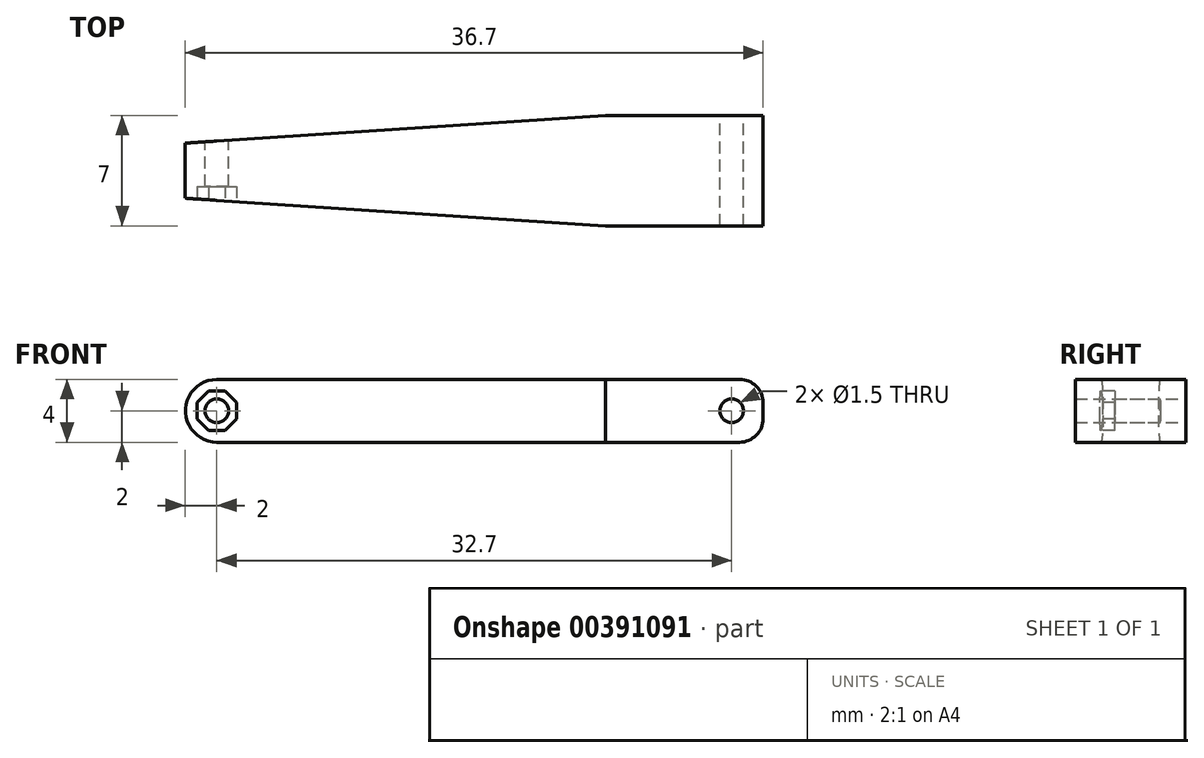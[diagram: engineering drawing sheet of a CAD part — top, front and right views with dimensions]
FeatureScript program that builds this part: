
annotation { "Feature Type Name" : "Feature", "Feature Type Description" : "" }
export const myFeature = defineFeature(function(context is Context, id is Id, definition is map)
    precondition{}
    {
        {
            var Q0;
            Q0=qCreatedBy(makeId("Top.planeOp"),FACE);
            var sketch = newSketch(context, id + "F0", { "sketchPlane" : qUnion([Q0])});
            skLineSegment(sketch, "E0.bottom", {"start": v(0, 0) * mm, "end": v(-36.7, 0) * mm});
            skLineSegment(sketch, "E0.top", {"start": v(0, -7) * mm, "end": v(-36.7, -7) * mm});
            skLineSegment(sketch, "E0.left", {"start": v(0, 0) * mm, "end": v(0, -7) * mm});
            skLineSegment(sketch, "E0.right", {"start": v(-36.7, 0) * mm, "end": v(-36.7, -7) * mm});
            skSolve(sketch);
        }
        {
            var Q0;
            Q0 = qSketchRegion(id + "F0", true);
            extrude(context, id + "F1", {"entities" : qUnion([Q0]), "depth" : 4 * mm});
        }
        {
            var Q0;
            Q0=makeQuery(id+"F1.opExtrude","CAP_FACE",FACE,{"disambiguationData":[OSD([sQuery(id+"F0.wireOp",EDGE,"E0.bottom"),sQuery(id+"F0.wireOp",EDGE,"E0.top"),sQuery(id+"F0.wireOp",EDGE,"E0.left"),sQuery(id+"F0.wireOp",EDGE,"E0.right")])],"isStart":false});
            var sketch = newSketch(context, id + "F2", { "sketchPlane" : qUnion([Q0])});
            skLineSegment(sketch, "E1", {"start": v(-36.7, -3.5) * mm, "end": v(0, -3.5) * mm, "construction": true});
            skLineSegment(sketch, "E2", {"start": v(0, 0) * mm, "end": v(-10, 0) * mm, "construction": true});
            skLineSegment(sketch, "E3", {"start": v(-36.7, -3.5) * mm, "end": v(-36.7, 0) * mm, "construction": true});
            skLineSegment(sketch, "E4", {"start": v(-36.7, -1.75) * mm, "end": v(-10, 0) * mm});
            skLineSegment(sketch, "E5.MirrorCS", {"start": v(-36.7, -5.25) * mm, "end": v(-10, -7) * mm});
            skLineSegment(sketch, "E6", {"start": v(-10, -7) * mm, "end": v(0, -7) * mm});
            skLineSegment(sketch, "E7", {"start": v(0, -7) * mm, "end": v(0, 0) * mm});
            skLineSegment(sketch, "E8", {"start": v(-36.7, -5.25) * mm, "end": v(-36.7, -1.75) * mm});
            skSolve(sketch);
        }
        {
            var Q0;
            Q0=makeQuery(id+"F1.opExtrude","SWEPT_FACE",FACE,{"disambiguationData":[OSD([sQuery(id+"F0.wireOp",EDGE,"E0.bottom")])]});
            var sketch = newSketch(context, id + "F3", { "sketchPlane" : qUnion([Q0])});
            skLineSegment(sketch, "E9", {"start": v(0, 2) * mm, "end": v(2, 2) * mm, "construction": true});
            skCircle(sketch, "E10", {"center": v(2, 2) * mm, "radius": 0.75 * mm});
            skSolve(sketch);
        }
        {
            var Q0;
            Q0=makeQuery(id+"F3.imprint","IMPRINT",FACE,{"disambiguationData":[TD([[makeQuery(id+"F3.imprint","IMPRINT",EDGE,{"derivedFrom":sQuery(id+"F3.wireOp",EDGE,"E10")}),1.0]])]});
            extrude(context, id + "F4", {"entities" : qUnion([Q0]), "operationType" : NewBodyOperationType.REMOVE, "oppositeDirection" : true, "depth" : 25 * mm});
        }
        {
            var Q0;
            Q0=makeQuery(id+"F1.opExtrude","CAP_EDGE",EDGE,{"disambiguationData":[OSD([sQuery(id+"F0.wireOp",EDGE,"E0.right")])],"isStart":true});
            var Q1;
            Q1=makeQuery(id+"F1.opExtrude","CAP_EDGE",EDGE,{"disambiguationData":[OSD([sQuery(id+"F0.wireOp",EDGE,"E0.right")])],"isStart":false});
            fillet(context, id + "F5", {"entities" : qUnion([Q0, Q1]), "radius" : 2 * mm, "tangentPropagation" : true, "allowEdgeOverflow" : false});
        }
        {
            var Q0;
            Q0=makeQuery(id+"F1.opExtrude","SWEPT_FACE",FACE,{"disambiguationData":[OSD([sQuery(id+"F0.wireOp",EDGE,"E0.bottom")])]});
            var sketch = newSketch(context, id + "F6", { "sketchPlane" : qUnion([Q0])});
            skLineSegment(sketch, "E11", {"start": v(36.7, 2) * mm, "end": v(34.7, 2) * mm, "construction": true});
            skCircle(sketch, "E12", {"center": v(34.7, 2) * mm, "radius": 0.75 * mm});
            skSolve(sketch);
        }
        {
            var Q0;
            Q0 = qSketchRegion(id + "F6", true);
            extrude(context, id + "F7", {"entities" : qUnion([Q0]), "operationType" : NewBodyOperationType.REMOVE, "oppositeDirection" : true, "depth" : 25 * mm});
        }
        {
            var Q0;
            Q0=makeQuery(id+"F1.opExtrude","CAP_EDGE",EDGE,{"disambiguationData":[OSD([sQuery(id+"F0.wireOp",EDGE,"E0.left")])],"isStart":false});
            var Q1;
            Q1=makeQuery(id+"F1.opExtrude","CAP_EDGE",EDGE,{"disambiguationData":[OSD([sQuery(id+"F0.wireOp",EDGE,"E0.left")])],"isStart":true});
            fillet(context, id + "F8", {"entities" : qUnion([Q0, Q1]), "radius" : 1.5 * mm, "tangentPropagation" : true, "allowEdgeOverflow" : false});
        }
        {
            var Q0;
            Q0=makeQuery(id+"F1.opExtrude","SWEPT_FACE",FACE,{"disambiguationData":[OSD([sQuery(id+"F0.wireOp",EDGE,"E0.top")])]});
            var sketch = newSketch(context, id + "F9", { "sketchPlane" : qUnion([Q0])});
            skPoint(sketch, "E13", {"position": v(-34.7, 2) * mm});
            skCircle(sketch, "E14.cCircle", {"center": v(-34.7, 2) * mm, "radius": 1.25 * mm, "construction": true});
            skLineSegment(sketch, "E14.0", {"start": v(-33.45, 2.52) * mm, "end": v(-33.45, 1.48) * mm});
            skLineSegment(sketch, "E14.1", {"start": v(-33.45, 1.48) * mm, "end": v(-34.18, 0.75) * mm});
            skLineSegment(sketch, "E14.2", {"start": v(-34.18, 0.75) * mm, "end": v(-35.22, 0.75) * mm});
            skLineSegment(sketch, "E14.3", {"start": v(-35.22, 0.75) * mm, "end": v(-35.95, 1.48) * mm});
            skLineSegment(sketch, "E14.4", {"start": v(-35.95, 1.48) * mm, "end": v(-35.95, 2.52) * mm});
            skLineSegment(sketch, "E14.5", {"start": v(-35.95, 2.52) * mm, "end": v(-35.22, 3.25) * mm});
            skLineSegment(sketch, "E14.6", {"start": v(-35.22, 3.25) * mm, "end": v(-34.18, 3.25) * mm});
            skLineSegment(sketch, "E14.7", {"start": v(-34.18, 3.25) * mm, "end": v(-33.45, 2.52) * mm});
            skPoint(sketch, "E14.0.midPoint", {"position": v(-33.45, 2) * mm});
            skSolve(sketch);
        }
        {
            var Q0;
            Q0=makeQuery(id+"F9.imprint","IMPRINT",FACE,{"disambiguationData":[TD([[makeQuery(id+"F9.imprint","IMPRINT",EDGE,{"derivedFrom":sQuery(id+"F9.wireOp",EDGE,"E14.0")}),-1.0]])]});
            extrude(context, id + "F10", {"entities" : qUnion([Q0]), "operationType" : NewBodyOperationType.REMOVE, "oppositeDirection" : true, "depth" : 2.5 * mm});
        }
        {
            var Q0;
            {var subQ0=sQuery(id+"F2.wireOp",EDGE,"E4");Q0=makeQuery(id+"F2.imprint","IMPRINT",FACE,{"disambiguationData":[TD([[makeQuery(id+"F2.imprint","IMPRINT",EDGE,{"derivedFrom":subQ0}),1.0]])]});}
            var Q1;
            {var subQ0=sQuery(id+"F2.wireOp",EDGE,"E5.MirrorCS");Q1=makeQuery(id+"F2.imprint","IMPRINT",FACE,{"disambiguationData":[TD([[makeQuery(id+"F2.imprint","IMPRINT",EDGE,{"derivedFrom":subQ0}),-1.0]])]});}
            extrude(context, id + "F11", {"entities" : qUnion([Q0, Q1]), "operationType" : NewBodyOperationType.REMOVE, "oppositeDirection" : true, "depth" : 25 * mm});
        }
    });
